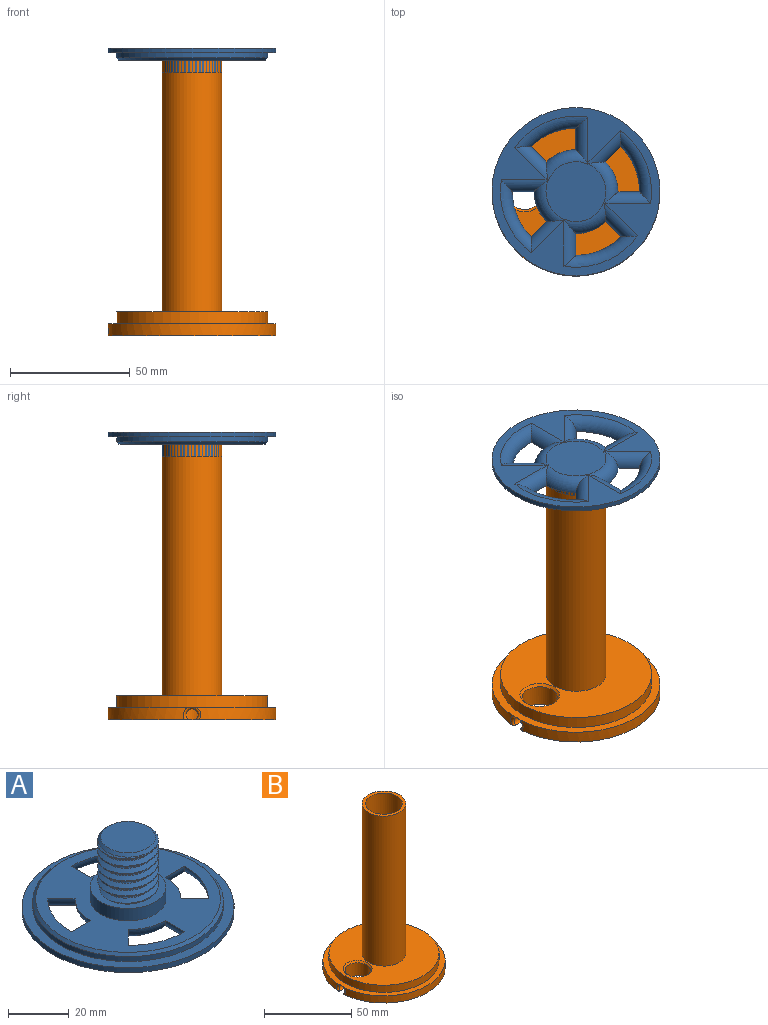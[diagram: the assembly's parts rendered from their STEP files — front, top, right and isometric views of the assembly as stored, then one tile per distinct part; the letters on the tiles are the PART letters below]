
ASSEMBLY  parts=2 mates=1
PART A: 36 faces, bbox 76.7x76.7x31.3 mm
  f0: plane 25x25mm, normal (0,0,-1), area 490.9mm2, adj f19,f20,f23,f24,f27,f28,f29,f32
  f1: cylinder r=35mm len=70mm, axis (0,0,-1), area 439.8mm2, adj f2,f3
  f2: plane 70x70mm, normal (0,0,1), area 731.2mm2, adj f1,f4
  f3: plane 70x70mm, normal (0,0,-1), area 1276.6mm2, adj f1,f16,f17,f18,f21,f22,f25,f26
  f4: cylinder r=31.5mm len=63mm, axis (0,0,-1), area 395.8mm2, adj f2,f15
  f5: plane 61x61mm, normal (0,0,1), area 1809.6mm2, adj f6,f15,f16,f17,f18,f19,f21,f22
  f6: cylinder r=12.5mm len=25mm, axis (0,0,-1), area 392.7mm2, adj f5,f7
  f7: plane 25.84x25.84mm, normal (0,0,1), area 231.8mm2, adj f6,f8,f11,f12,f13
  f8: cylinder r=10mm len=20mm, axis (0,0,-1), area 116.1mm2, adj f7,f10,f12,f13
  f9: plane 18x18mm, normal (0,0,1), area 254.5mm2, adj f10
  f10: cone r=9mm half-angle=45deg, axis (0,0,-1), area 84.4mm2, adj f8,f9,f14
  f11: bspline ~21.25x19.34mm, area 277.5mm2, adj f7,f12,f13,f14
  f12: bspline ~23.09x21.44mm, area 686.6mm2, adj f7,f8,f11,f14
  f13: bspline ~23.09x21.44mm, area 684.4mm2, adj f7,f8,f11,f14
  f14: plane 20.84x20.84mm, normal (0,0,-1), area 55mm2, adj f10,f11,f12,f13
  f15: cone r=30.5mm half-angle=45deg, axis (0,0,-1), area 275.5mm2, adj f4,f5
  f16: torus R=31.5mm, axis (0,0,1), area 211.2mm2, adj f3,f5,f17,f18
  f17: cylinder r=5mm len=19.41mm, axis (0,1,0), area 100.1mm2, adj f3,f5,f16,f19,f21
  f18: cylinder r=5mm len=17.26mm, axis (-0.71,-0.71,0), area 100.1mm2, adj f3,f5,f16,f19,f22
  f19: torus R=12.5mm, axis (0,0,1), area 125.5mm2, adj f0,f5,f17,f18,f20,f23
  f20: torus R=12.5mm, axis (0,0,1), area 0mm2, adj f0,f19,f24
  f21: cylinder r=5mm len=17.26mm, axis (0.71,-0.71,0), area 100.1mm2, adj f3,f5,f17,f24,f25
  f22: cylinder r=5mm len=19.41mm, axis (1,0,0), area 100.1mm2, adj f3,f5,f18,f26,f27
  f23: torus R=12.5mm, axis (0,0,1), area 0mm2, adj f0,f19,f27
  f24: torus R=12.5mm, axis (0,0,1), area 125.5mm2, adj f0,f5,f20,f21,f29,f30
  f25: torus R=31.5mm, axis (0,0,1), area 211.2mm2, adj f3,f5,f21,f30
  f26: torus R=31.5mm, axis (0,0,1), area 211.2mm2, adj f3,f5,f22,f31
  f27: torus R=12.5mm, axis (0,0,1), area 125.5mm2, adj f0,f5,f22,f23,f28,f31
  f28: torus R=12.5mm, axis (0,0,1), area 0mm2, adj f0,f27,f32
  f29: torus R=12.5mm, axis (0,0,1), area 0mm2, adj f0,f24,f32
  f30: cylinder r=5mm len=19.41mm, axis (-1,0,0), area 100.1mm2, adj f3,f5,f24,f25,f33
  f31: cylinder r=5mm len=17.26mm, axis (-0.71,0.71,0), area 100.1mm2, adj f3,f5,f26,f27,f34
  f32: torus R=12.5mm, axis (0,0,1), area 125.5mm2, adj f0,f5,f28,f29,f33,f34
  f33: cylinder r=5mm len=17.26mm, axis (0.71,0.71,0), area 100.1mm2, adj f3,f5,f30,f32,f35
  f34: cylinder r=5mm len=19.41mm, axis (0,-1,0), area 100.1mm2, adj f3,f5,f31,f32,f35
  f35: torus R=31.5mm, axis (0,0,1), area 211.2mm2, adj f3,f5,f33,f34
PART B: 13 faces, bbox 71.3x71.3x117.5 mm
  f0: cylinder r=35mm len=70mm, axis (0,0,-1), area 1066.7mm2, adj f1,f2,f10
  f1: plane 70x69.88mm, normal (0,0,-1), area 3663.4mm2, adj f0,f7,f8,f10
  f2: plane 71.28x71.23mm, normal (0,0,1), area 730.8mm2, adj f0,f3,f10
  f3: cylinder r=31.5mm len=63mm, axis (0,0,-1), area 989.6mm2, adj f2,f4
  f4: plane 63x63mm, normal (0,0,1), area 2412.7mm2, adj f3,f6,f9
  f5: plane 25x25mm, normal (0,0,1), area 144.5mm2, adj f6,f11
  f6: cylinder r=12.5mm len=105mm, axis (0,0,-1), area 8246.7mm2, adj f4,f5
  f7: cylinder r=2.55mm len=5.49mm, axis (-1,0,0), area 70.2mm2, adj f1,f8,f10
  f8: cylinder r=7.25mm len=14.49mm, axis (0,0,1), area 390.1mm2, adj f1,f7,f9
  f9: cone r=7.25mm half-angle=45deg, axis (0,0,1), area 68.8mm2, adj f4,f8
  f10: bspline ~7.32x6.81mm, area 22.6mm2, adj f0,f1,f2,f7
  f11: cylinder r=10.5mm len=100mm, axis (0,0,1), area 6597.3mm2, adj f5,f12
  f12: plane 21x21mm, normal (0,0,1), area 346.4mm2, adj f11
PLACE A rot(axis=(-0.71,0.71,0),180deg) t=(-25.48,-19.59,144.97)mm
PLACE B t=(-25.48,-19.59,24.97)mm
MATE slider A.f8 <-> B.f11  axis (0,0,-1) through (-25.48,-19.59,114.97)mm
